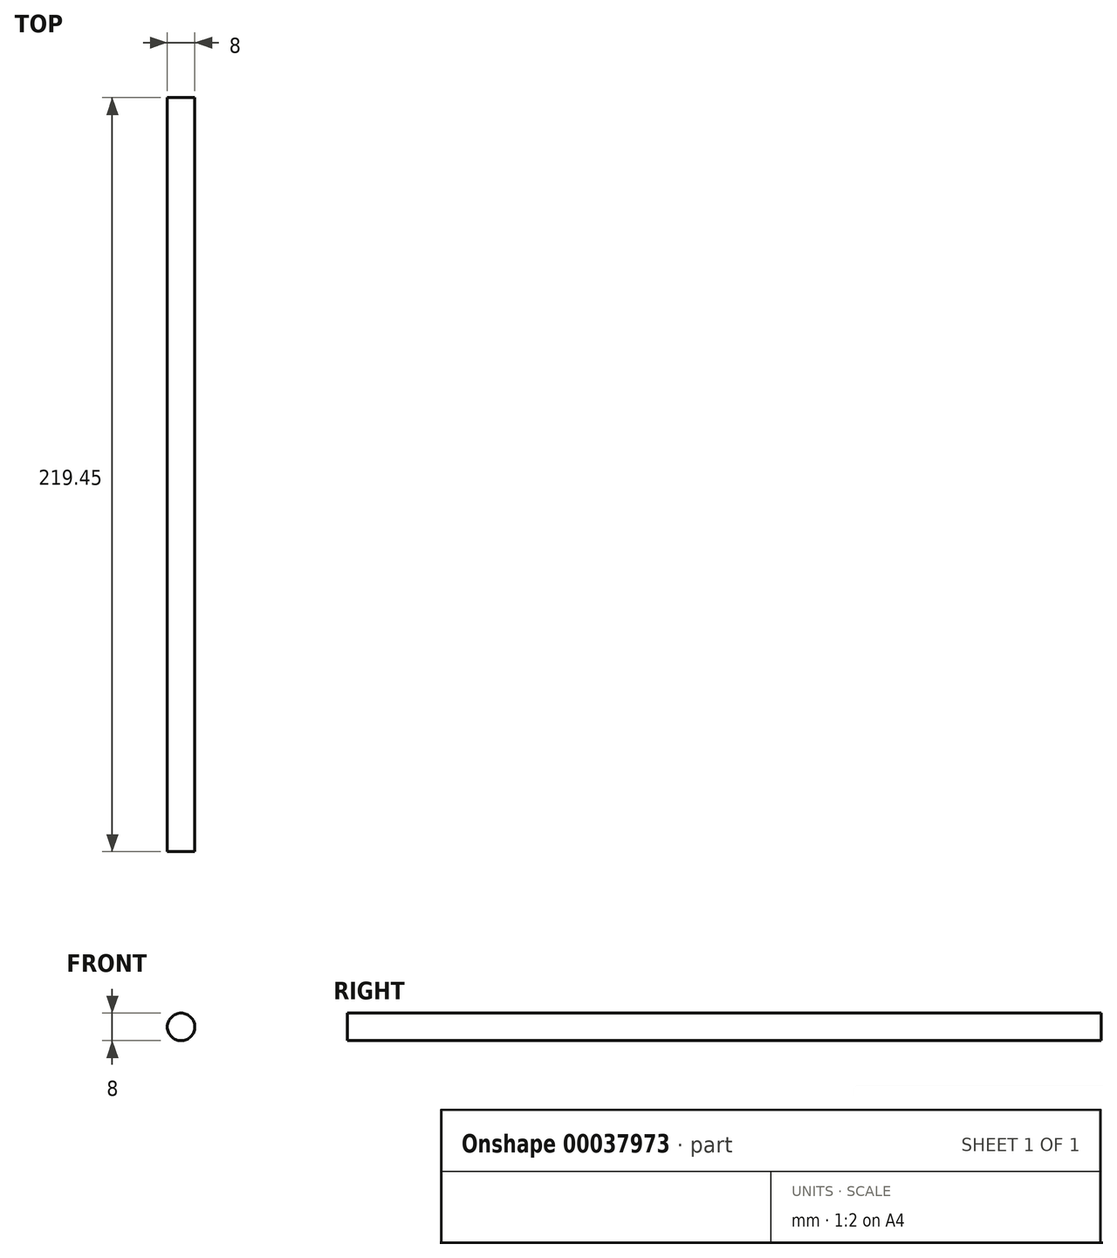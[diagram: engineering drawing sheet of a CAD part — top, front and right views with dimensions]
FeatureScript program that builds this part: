
annotation { "Feature Type Name" : "Feature", "Feature Type Description" : "" }
export const myFeature = defineFeature(function(context is Context, id is Id, definition is map)
    precondition{}
    {
        {
            var Q0;
            Q0=qCreatedBy(makeId("Front.planeOp"),FACE);
            var sketch = newSketch(context, id + "F0", { "sketchPlane" : qUnion([Q0])});
            skCircle(sketch, "E0", {"center": v(0, 0) * mm, "radius": 4 * mm});
            skSolve(sketch);
        }
        {
            var Q0;
            Q0=qSketchRegion(id+"F0",true);
            extrude(context, id + "F1", {"entities" : qUnion([Q0]), "depth" : 219.45 * mm});
        }
    });
